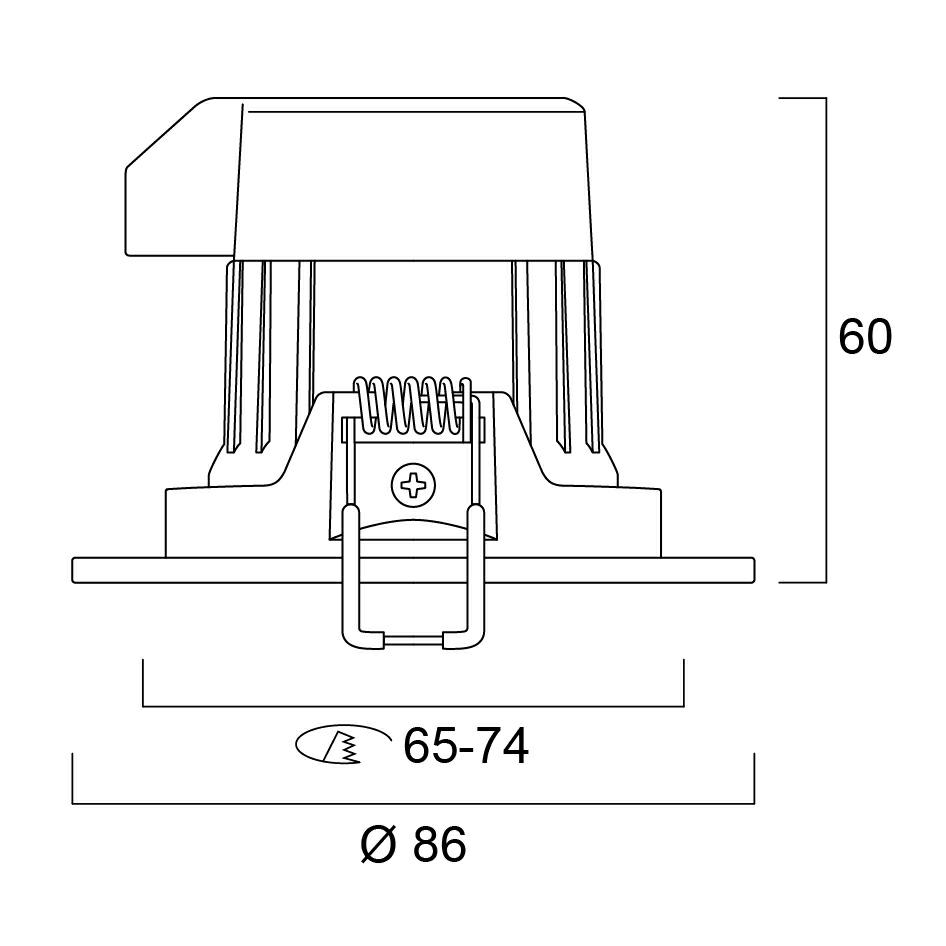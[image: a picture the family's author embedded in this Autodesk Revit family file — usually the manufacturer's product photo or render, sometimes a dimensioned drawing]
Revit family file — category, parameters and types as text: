
# Revit family: 5184
name_source: partatom
category: Lighting Fixtures
revit_build: Autodesk Revit 2018 (Build: 20170223_1515(x64)
units: mm (PartAtom-declared; Revit-internal decimal feet)

## family parameters
Cut with Voids When Loaded = No
Host = Face
Light Source = No
OmniClass Number = 23.80.70.00
OmniClass Title = Lighting
Part Type = Normal
Room Calculation Point = No
Round Connector Dimension = Use Diameter
Shared = No

## types (1)
- 0005184 START SPOT ALU 870LM 3CCT DIM IP44 WHT
    Apparent Load = 9 VA
    Assembly Code = D5020200
    AssetType = Fixed
    ClassificationName = Uniclass2015
    ClassificationValue = EF_70_80
    Cost = 0 $
    Default Elevation = 1219 mm
    DepthDiffuser_FEILO = 5 mm  [stored 0.0164042 ft]
    Description = Integrated LED recessed spotlight, vertical tilt 30°, white aluminium bezel finish, dimmable trailing/leading edge, 3-CCT changeable 2700-3000-4000K, 50° degree beam angle, polycarbonate and aluminium body, low profile 62mm recessed depth, IP44 from the front, IK03, loop-in/loop-out terminals for fast wiring, 68-72mm cutout, clear lens. Additional black or gold reflectors  can be ordered as accessory.
    DiameterBezel_FEILO = 86 mm  [stored 0.282152 ft]
    DocumentationLiterature = http://www.sylvania-lighting.com
    DurationUnit = hours
    ElectricShockClassification = 100
    ExpectedLife = 50000
    HeightBezel_FEILO = 2 mm  [stored 0.00656168 ft]
    IfcExportAs = Class II
    IfcExportType = IfcLightFixtureType
    ImpactProtectionIndex = IfcLightFixtureType
    IngressProtection = IfcLightFixtureType
    InputNominalFrequency = 3000
    InputVoltage = 0
    LampColourRenderingIndex = 16500
    LampColourTemperature = LED
    LampMacAdamStep = 80
    LampNominalLuminous = 3000 K
    LightOutputRatio = LED
    LuminaireType = 0
    ManufacturerName = 100 lm/W
    Material = Feilo Sylvania
    Material_1_FEILO = Body-Sylvania-StartSpot-White
    Material_2_FEILO = LED-Sylvania-StartSpot
    Material_3_FEILO = <By Category>
    Material_4_FEILO = <By Category>
    Model = START SPOT ALU 870LM 3CCT DIM IP44 WHT
    ModelNumber = 0005184
    ModelReference = START SPOT ALU 870LM 3CCT DIM IP44 WHT
    Name = START SPOT ALU 870LM 3CCT DIM IP44 WHT
    NominalDepth = 86 mm  [stored 0.282152 ft]
    NominalHeight = 60 mm  [stored 0.19685 ft]
    NominalLength = 86 mm  [stored 0.282152 ft]
    PowerConsumption = Lighting
    PowerFactor = 0
    RadiusCutout_FEILO = 36 mm
    RadiusDiffuser_FEILO = 14 mm  [stored 0.0459318 ft]
    RadiusOptics_FEILO = 99 mm
    Type Image = <None>
    TypeHead_FEILO = Start Spot IP20 Head : 0005184 START SPOT ALU 870LM 3CCT DIM IP44 WHT
    TypeName = START SPOT ALU 870LM 3CCT DIM IP44 WHT
    URL = 0.9
    VisibilityTop_FEILO = Yes
    Voltage = 230 V
    WarrantyDescription = http://www.sylvania-lighting.com

note: [stored X ft] marks values corroborated as IEEE doubles in the binary element streams (Revit-internal decimal feet)

## geometry (parser evidence)
native form markers: Sweep x8
no freeform markers — native parametric forms only
